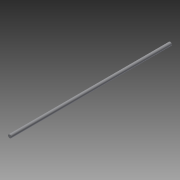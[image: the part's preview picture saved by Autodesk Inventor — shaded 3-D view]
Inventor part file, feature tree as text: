
AUTODESK INVENTOR PART (.ipt)
format: ipt  version: 2015 (Build 190159000, 159)  size: 65,024 bytes
history: native  units: mm
features: extrude x1, sketch x1
ambient origin geometry x8: Origin, YZ Plane, XZ Plane, XY Plane, X Axis, Y Axis, Z Axis, Center Point
bodies: Solid1 (feature_tree)
feature tree (2):
  extrude  "Extrusion1"  Depth=380.0mm TaperAngle=0.0deg
  sketch  "Sketch2"  dims[d1=8.0mm d2=380.0mm d3=0.0mm]
